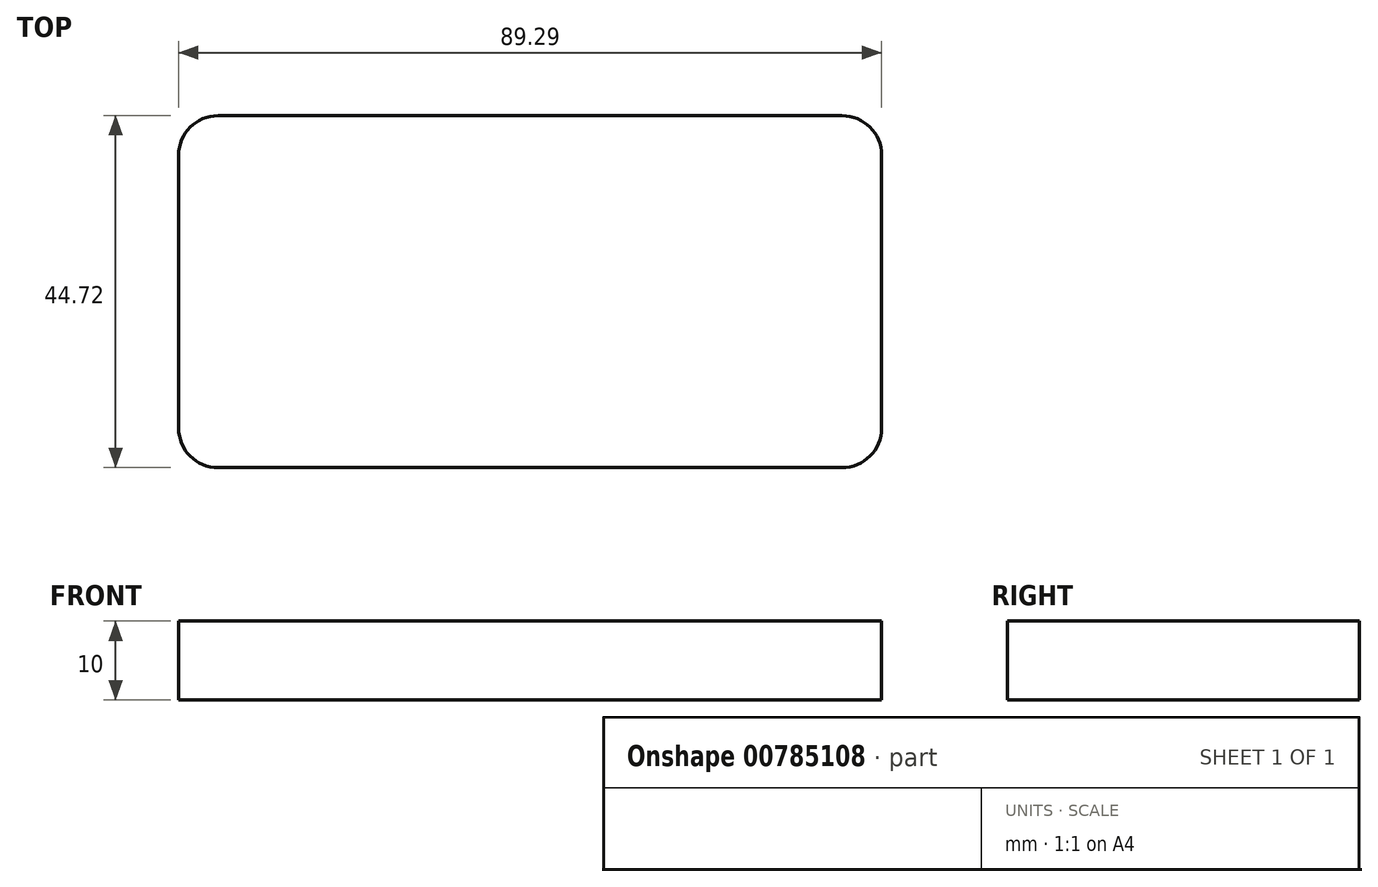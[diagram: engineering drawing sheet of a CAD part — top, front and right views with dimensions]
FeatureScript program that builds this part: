
annotation { "Feature Type Name" : "Feature", "Feature Type Description" : "" }
export const myFeature = defineFeature(function(context is Context, id is Id, definition is map)
    precondition{}
    {
        {
            var Q0;
            Q0=qCreatedBy(makeId("Top.planeOp"),FACE);
            var sketch = newSketch(context, id + "F0", { "sketchPlane" : qUnion([Q0])});
            skLineSegment(sketch, "E0.bottom", {"start": v(5, 0) * mm, "end": v(84.29, 0) * mm});
            skLineSegment(sketch, "E0.top", {"start": v(5, -44.72) * mm, "end": v(84.29, -44.72) * mm});
            skLineSegment(sketch, "E0.left", {"start": v(0, -5) * mm, "end": v(0, -39.72) * mm});
            skLineSegment(sketch, "E0.right", {"start": v(89.29, -5) * mm, "end": v(89.29, -39.72) * mm});
            skPoint(sketch, "E1.visualSharp", {"position": v(0, 0) * mm});
            skArc(sketch, "E1.filletArc", {"start": v(5, 0) * mm, "mid": v(1.46, -1.46) * mm, "end": v(0, -5) * mm});
            skPoint(sketch, "E2.visualSharp", {"position": v(0, -44.72) * mm});
            skArc(sketch, "E2.filletArc", {"start": v(0, -39.72) * mm, "mid": v(1.46, -43.25) * mm, "end": v(5, -44.72) * mm});
            skPoint(sketch, "E3.visualSharp", {"position": v(89.29, 0) * mm});
            skArc(sketch, "E3.filletArc", {"start": v(89.29, -5) * mm, "mid": v(87.82, -1.46) * mm, "end": v(84.29, 0) * mm});
            skPoint(sketch, "E4.visualSharp", {"position": v(89.29, -44.72) * mm});
            skArc(sketch, "E4.filletArc", {"start": v(84.29, -44.72) * mm, "mid": v(87.82, -43.25) * mm, "end": v(89.29, -39.72) * mm});
            skSolve(sketch);
        }
        {
            var Q0;
            Q0 = qSketchRegion(id + "F0", true);
            extrude(context, id + "F1", {"entities" : qUnion([Q0]), "depth" : 10 * mm, "offsetDistance" : 25 * mm});
        }
    });
